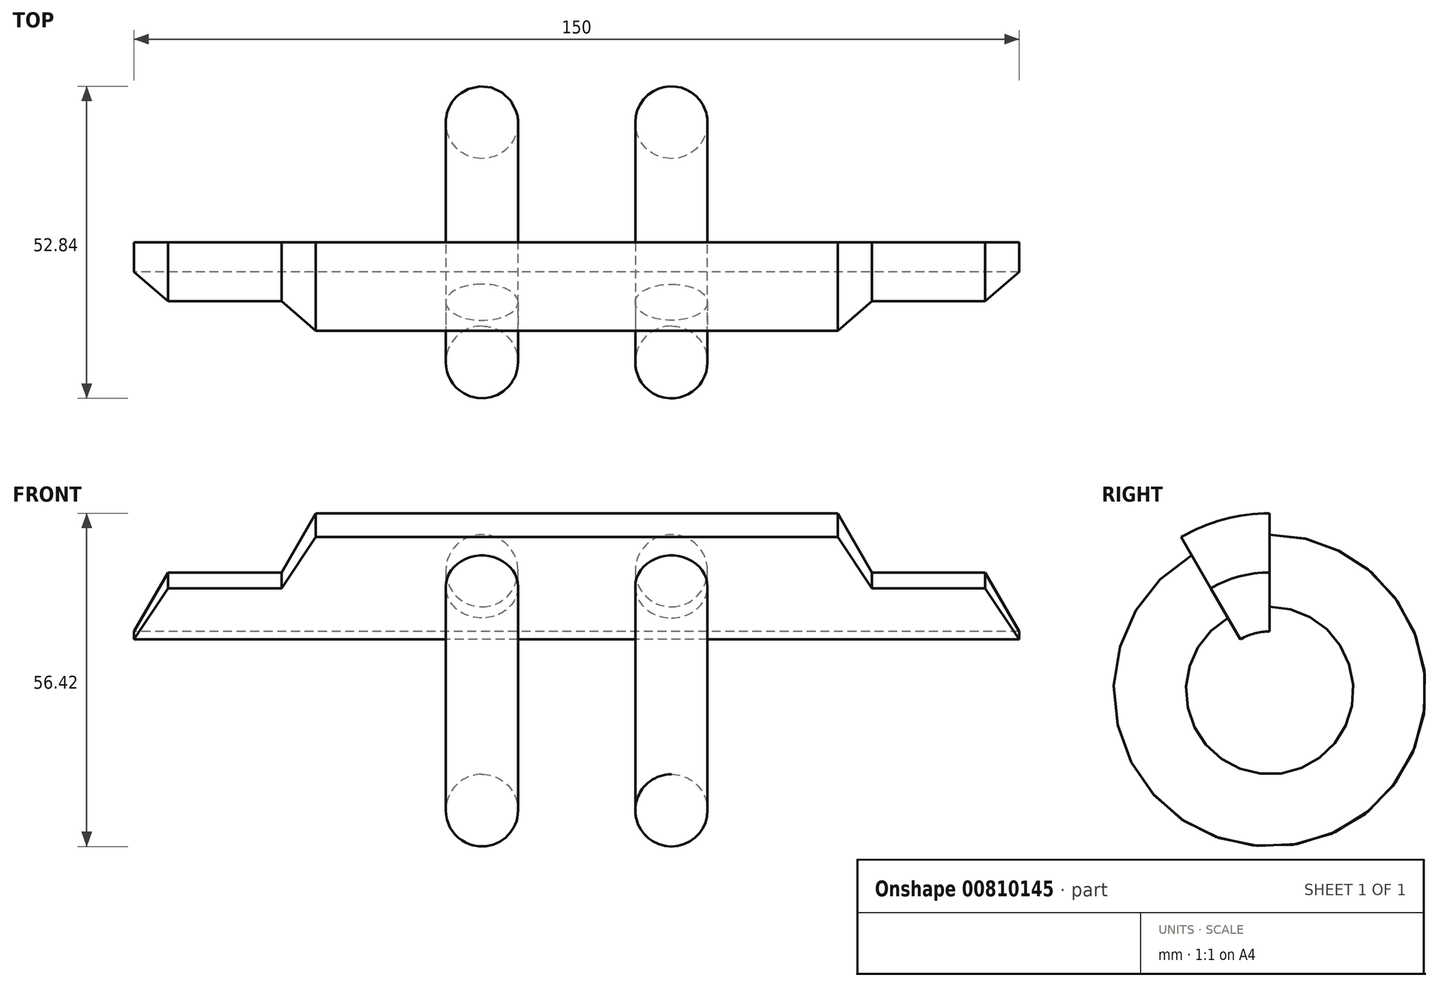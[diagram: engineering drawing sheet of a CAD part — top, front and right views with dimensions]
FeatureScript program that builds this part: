
annotation { "Feature Type Name" : "Feature", "Feature Type Description" : "" }
export const myFeature = defineFeature(function(context is Context, id is Id, definition is map)
    precondition{}
    {
        {
            var Q0;
            Q0=qCreatedBy(makeId("Front.planeOp"),FACE);
            var sketch = newSketch(context, id + "F0", { "sketchPlane" : qUnion([Q0])});
            skLineSegment(sketch, "E0", {"start": v(-50, 30) * mm, "end": v(-5.77, 30) * mm});
            skLineSegment(sketch, "E1", {"start": v(-5.77, 30) * mm, "end": v(0, 20) * mm});
            skLineSegment(sketch, "E2", {"start": v(0, 20) * mm, "end": v(19.23, 20) * mm});
            skLineSegment(sketch, "E3", {"start": v(19.23, 20) * mm, "end": v(25, 10) * mm});
            skLineSegment(sketch, "E4", {"start": v(25, 10) * mm, "end": v(-50, 10) * mm});
            skLineSegment(sketch, "E5", {"start": v(-50, 10) * mm, "end": v(-50, 30) * mm});
            skLineSegment(sketch, "E6", {"start": v(-50, 0) * mm, "end": v(25, 0) * mm, "construction": true});
            skSolve(sketch);
        }
        {
            var Q0;
            Q0 = qSketchRegion(id + "F0", true);
            var Q1;
            Q1=sQuery(id+"F0.wireOp",EDGE,"E6");
            revolve(context, id + "F1", {"surfaceOperationType" : NewSurfaceOperationType.NEW, "entities" : qUnion([Q0]), "axis" : qUnion([Q1]), "revolveType" : RevolveType.ONE_DIRECTION, "angle" : 30 * degree});
        }
        {
            var Q0;
            Q0=makeQuery(id+"F1.opRevolve","CAP_FACE",FACE,{"disambiguationData":[OSD([sQuery(id+"F0.wireOp",EDGE,"E0"),sQuery(id+"F0.wireOp",EDGE,"E1"),sQuery(id+"F0.wireOp",EDGE,"E2"),sQuery(id+"F0.wireOp",EDGE,"E3"),sQuery(id+"F0.wireOp",EDGE,"E4"),sQuery(id+"F0.wireOp",EDGE,"E5")])],"isStart":false});
            var sketch = newSketch(context, id + "F2", { "sketchPlane" : qUnion([Q0])});
            skCircle(sketch, "E7", {"center": v(-33.95, 20.3) * mm, "radius": 6.12 * mm});
            skLineSegment(sketch, "E8", {"start": v(72.85, 0) * mm, "end": v(-62.45, 0) * mm, "construction": true});
            skSolve(sketch);
        }
        {
            var Q0;
            Q0 = qSketchRegion(id + "F2", true);
            var Q1;
            Q1=sQuery(id+"F2.wireOp",EDGE,"E8");
            revolve(context, id + "F3", {"operationType" : NewBodyOperationType.ADD, "surfaceOperationType" : NewSurfaceOperationType.NEW, "entities" : qUnion([Q0]), "axis" : qUnion([Q1]), "revolveType" : RevolveType.FULL, "oppositeDirection" : true});
        }
        {
            var Q0;
            Q0=makeQuery(id+"F1.opRevolve","SWEPT_BODY",BODY,{"disambiguationData":[OSD([sQuery(id+"F0.wireOp",EDGE,"E0"),sQuery(id+"F0.wireOp",EDGE,"E1"),sQuery(id+"F0.wireOp",EDGE,"E2"),sQuery(id+"F0.wireOp",EDGE,"E3"),sQuery(id+"F0.wireOp",EDGE,"E4"),sQuery(id+"F0.wireOp",EDGE,"E5")])]});
            var Q1;
            Q1=makeQuery(id+"F1.opRevolve","SWEPT_FACE",FACE,{"disambiguationData":[OSD([sQuery(id+"F0.wireOp",EDGE,"E5")])]});
            mirror(context, id + "F4", {"operationType" : NewBodyOperationType.ADD, "entities" : qUnion([Q0]), "mirrorPlane" : qUnion([Q1])});
        }
    });
